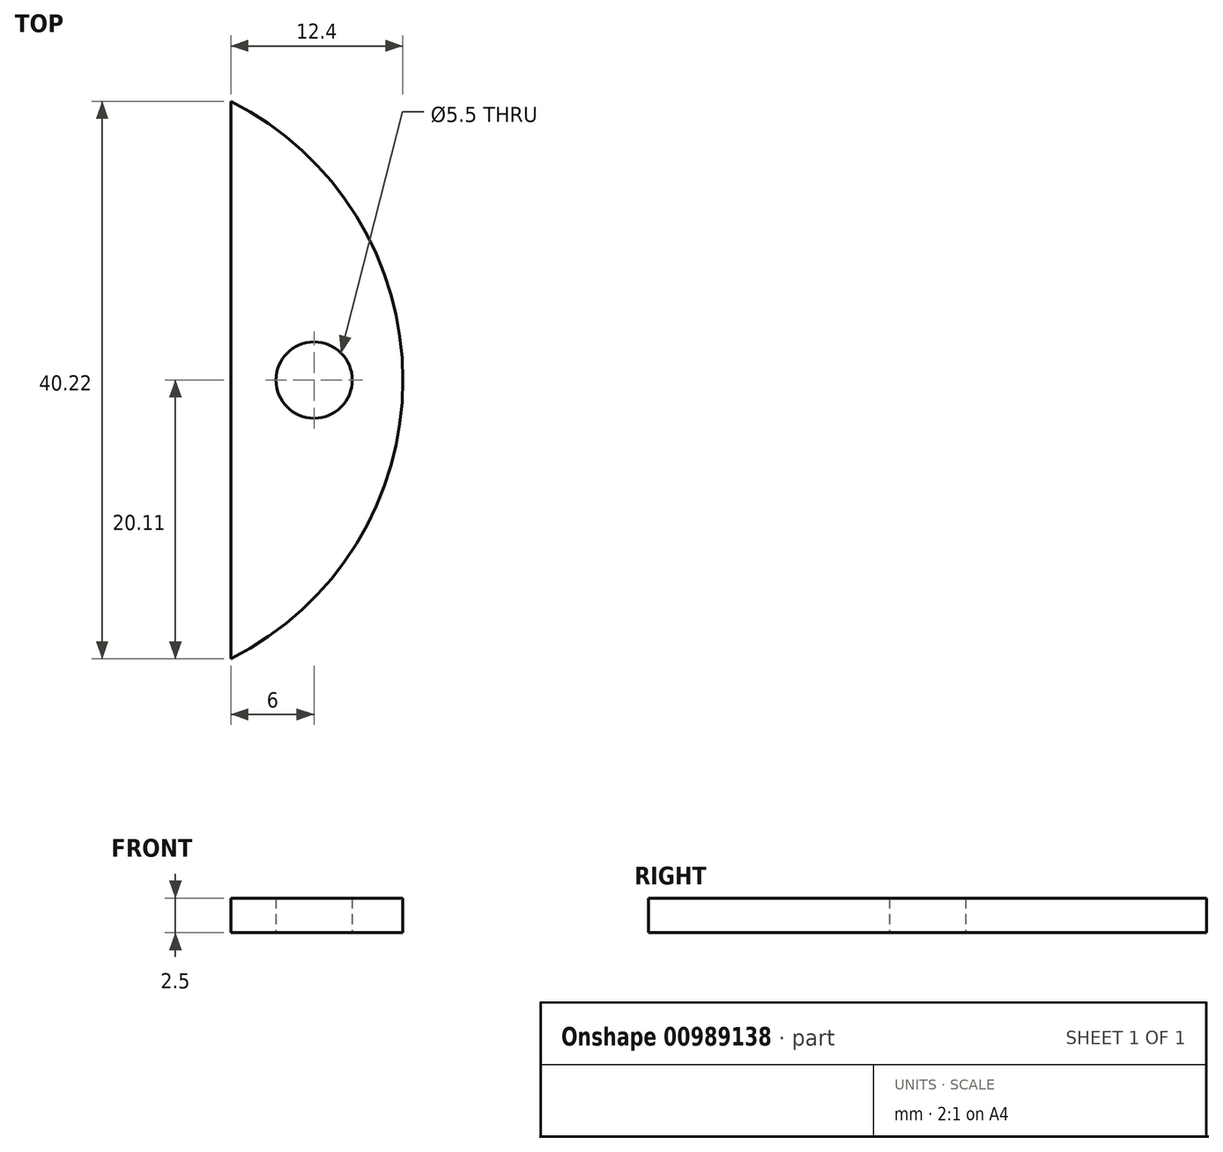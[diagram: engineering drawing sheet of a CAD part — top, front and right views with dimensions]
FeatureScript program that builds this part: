
annotation { "Feature Type Name" : "Feature", "Feature Type Description" : "" }
export const myFeature = defineFeature(function(context is Context, id is Id, definition is map)
    precondition{}
    {
        {
            var Q0;
            Q0=qCreatedBy(makeId("Top.planeOp"),FACE);
            var sketch = newSketch(context, id + "F0", { "sketchPlane" : qUnion([Q0])});
            skArc(sketch, "E0", {"start": v(10.1, -20.1) * mm, "mid": v(22.5, 0) * mm, "end": v(10.1, 20.1) * mm});
            skLineSegment(sketch, "E1", {"start": v(10.1, -20.1) * mm, "end": v(10.1, 20.1) * mm});
            skPoint(sketch, "E2.centerSnap0", {"position": v(10.1, 0) * mm});
            skCircle(sketch, "E3", {"center": v(16.1, 0) * mm, "radius": 2.75 * mm});
            skSolve(sketch);
        }
        {
            var Q0;
            Q0=makeQuery(id+"F0.imprint","IMPRINT",FACE,{"disambiguationData":[TD([[makeQuery(id+"F0.imprint","IMPRINT",EDGE,{"derivedFrom":sQuery(id+"F0.wireOp",EDGE,"E0")}),1.0]])]});
            extrude(context, id + "F1", {"entities" : qUnion([Q0]), "depth" : 2.5 * mm, "offsetDistance" : 25.4 * mm});
        }
    });
